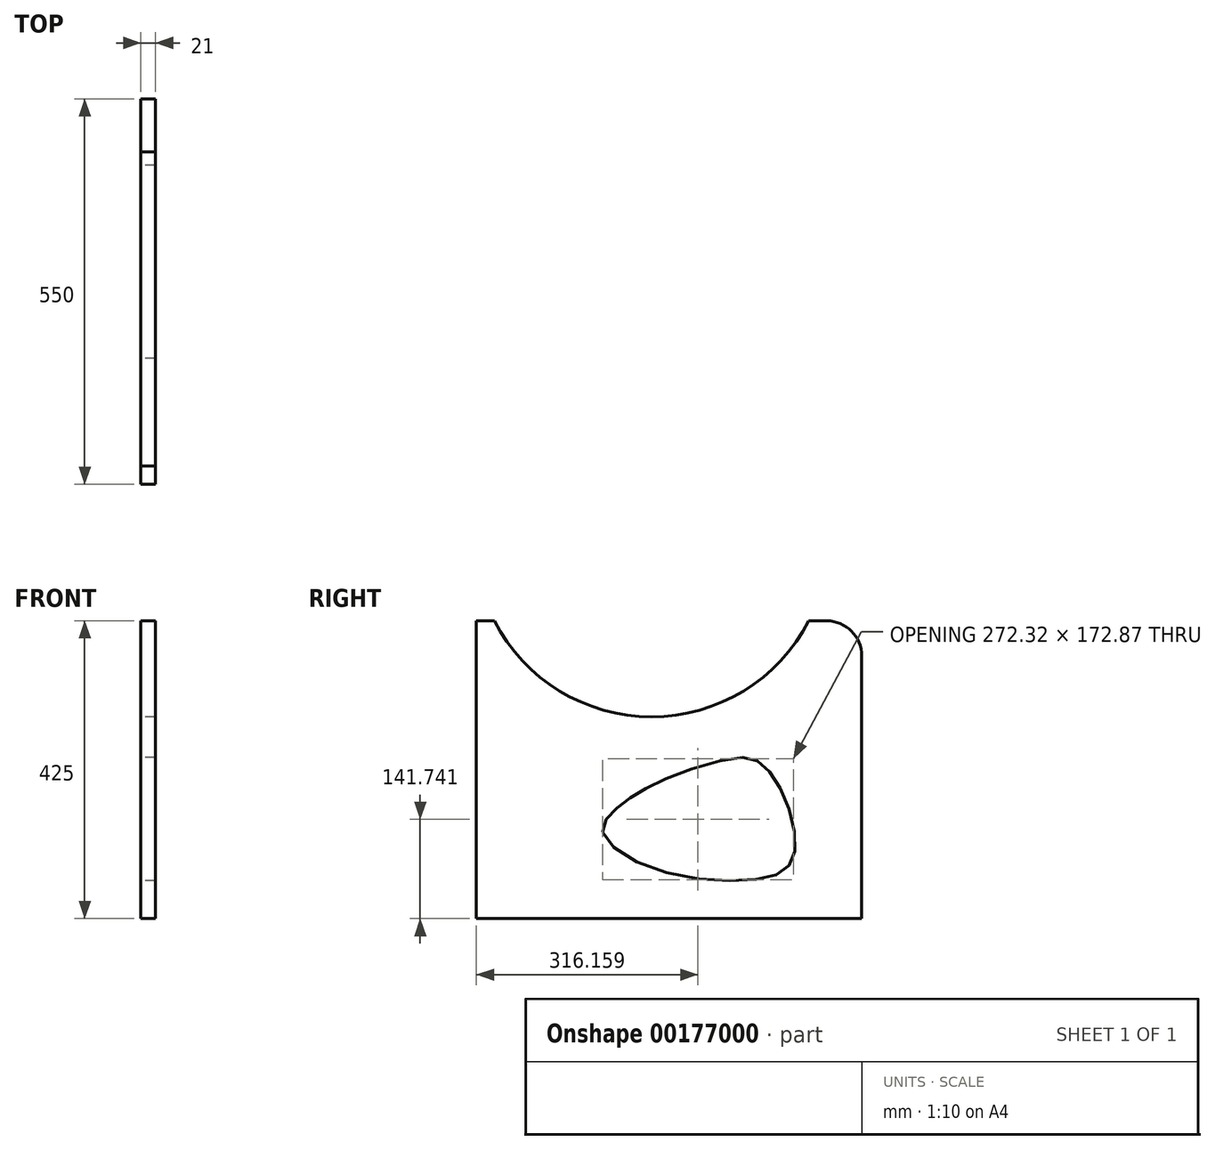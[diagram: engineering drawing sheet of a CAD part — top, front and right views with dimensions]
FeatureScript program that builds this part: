
annotation { "Feature Type Name" : "Feature", "Feature Type Description" : "" }
export const myFeature = defineFeature(function(context is Context, id is Id, definition is map)
    precondition{}
    {
        {
            var Q0;
            Q0=qCreatedBy(makeId("Right.planeOp"),FACE);
            var sketch = newSketch(context, id + "F0", { "sketchPlane" : qUnion([Q0])});
            skLineSegment(sketch, "E0.bottom", {"start": v(0, 0) * mm, "end": v(550, 0) * mm});
            skLineSegment(sketch, "E0.top", {"start": v(0, 425) * mm, "end": v(25.77, 425) * mm});
            skLineSegment(sketch, "E0.left", {"start": v(0, 0) * mm, "end": v(0, 425) * mm});
            skLineSegment(sketch, "E0.right", {"start": v(550, 0) * mm, "end": v(550, 375) * mm});
            skPoint(sketch, "E1.visualSharp", {"position": v(550, 425) * mm});
            skArc(sketch, "E1.filletArc", {"start": v(550, 375) * mm, "mid": v(535.36, 410.36) * mm, "end": v(500, 425) * mm});
            skArc(sketch, "E2", {"start": v(25.77, 425) * mm, "mid": v(250, 288) * mm, "end": v(474.23, 425) * mm});
            skLineSegment(sketch, "E3.trimOffspring", {"start": v(474.23, 425) * mm, "end": v(500, 425) * mm});
            skLineSegment(sketch, "E4.bottom", {"start": v(455, 55) * mm, "end": v(180, 55) * mm, "construction": true});
            skLineSegment(sketch, "E4.top", {"start": v(455, 230) * mm, "end": v(180, 230) * mm, "construction": true});
            skLineSegment(sketch, "E4.left", {"start": v(455, 55) * mm, "end": v(455, 230) * mm, "construction": true});
            skLineSegment(sketch, "E4.right", {"start": v(180, 55) * mm, "end": v(180, 230) * mm, "construction": true});
            skFitSpline(sketch, "E5", {"points": [v(180, 123.44) * mm, v(191.13, 148.56) * mm, v(220.86, 173.27) * mm, v(278.21, 202.57) * mm, v(379.12, 230) * mm, v(409.68, 218.9) * mm, v(440.66, 171.6) * mm, v(455, 101.67) * mm, v(440.66, 70.27) * mm, v(386.65, 55) * mm, v(248.49, 72.78) * mm, v(180, 123.44) * mm]});
            skSolve(sketch);
        }
        {
            var Q0;
            Q0=makeQuery(id+"F0.imprint","IMPRINT",FACE,{"disambiguationData":[TD([[makeQuery(id+"F0.imprint","IMPRINT",EDGE,{"derivedFrom":sQuery(id+"F0.wireOp",EDGE,"E0.bottom")}),1.0]])]});
            extrude(context, id + "F1", {"entities" : qUnion([Q0]), "depth" : 21 * mm});
        }
    });
